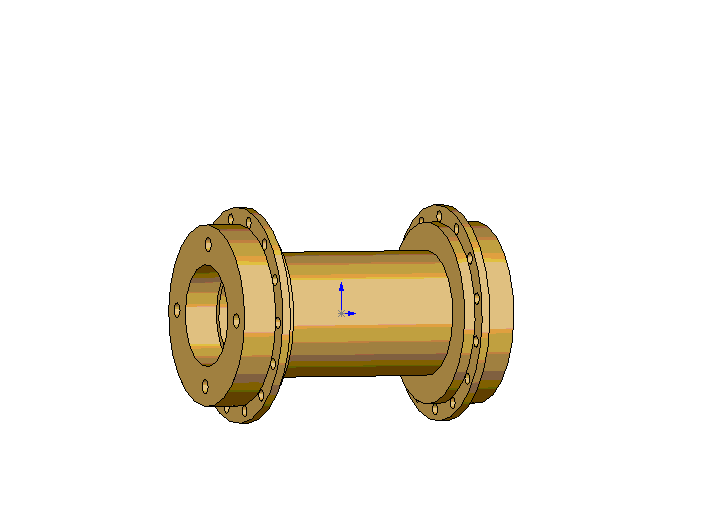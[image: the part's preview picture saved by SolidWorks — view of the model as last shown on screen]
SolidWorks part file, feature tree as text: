
SOLIDWORKS PART (.sldprt)
format: sldprt  version: not decoded by parser v0  size: 482,816 bytes
history: native  units: mm
features: sketch x7, thread x4, hole x3, material x1, revolve x1 (+12 scaffold rows collapsed)
feature tree (28):
  scaffold x12  (default folders/planes/origin — collapsed)
  material  "Material <not specified>"
  sketch  "Sketch1"  dims[D1=63.5mm D2=2.3622mm D3=60.325mm D4=25.4mm D5=28.575mm D6=9.525mm D7=9.525mm D8=50.8mm D9=34.925mm D10=3.175mm]
  revolve  "Revolve1"  Angle=360deg
  hole  "#10-32 Tapped Hole1"  [1 undecoded]
  sketch  "Sketch3"
  thread  "Cosmetic Thread1"  Diameter=4.826mm  [1 undecoded]
  thread  "Cosmetic Thread2"  Diameter=4.826mm  [1 undecoded]
  thread  "Cosmetic Thread3"  Diameter=4.826mm  [1 undecoded]
  thread  "Cosmetic Thread4"  Diameter=4.826mm  [1 undecoded]
  sketch  "Sketch2"  dims[hole-wizard template sketch: 60 standard entries collapsed; hole parameters kept: c18.Thru Tap Drill Depth=15.0622mm]
  hole  "1/8 (0.125000) Diameter Hole1"  Diameter=3.175mm Depth=2.3622mm
  sketch  "Sketch5"  dims[D1=26.9748mm]
  sketch  "Sketch4"  dims[hole-wizard template sketch: 60 standard entries collapsed; hole parameters kept: c18.Thru Hole Depth=2.3622mm]
  hole  "1/8 (0.125000) Diameter Hole2"  Diameter=3.175mm Depth=2.3622mm
  sketch  "Sketch7"  dims[D1=26.9748mm]
  sketch  "Sketch6"  dims[hole-wizard template sketch: 60 standard entries collapsed; hole parameters kept: c18.Thru Hole Depth=2.3622mm]
decode coverage: 13 of 15 modeling features carry decoded parameters
note: ~ marks probable driven/reference dimensions
note: 5 parameter values undecoded
note: suppression state not decoded; provenance and decode notes live in map.json
